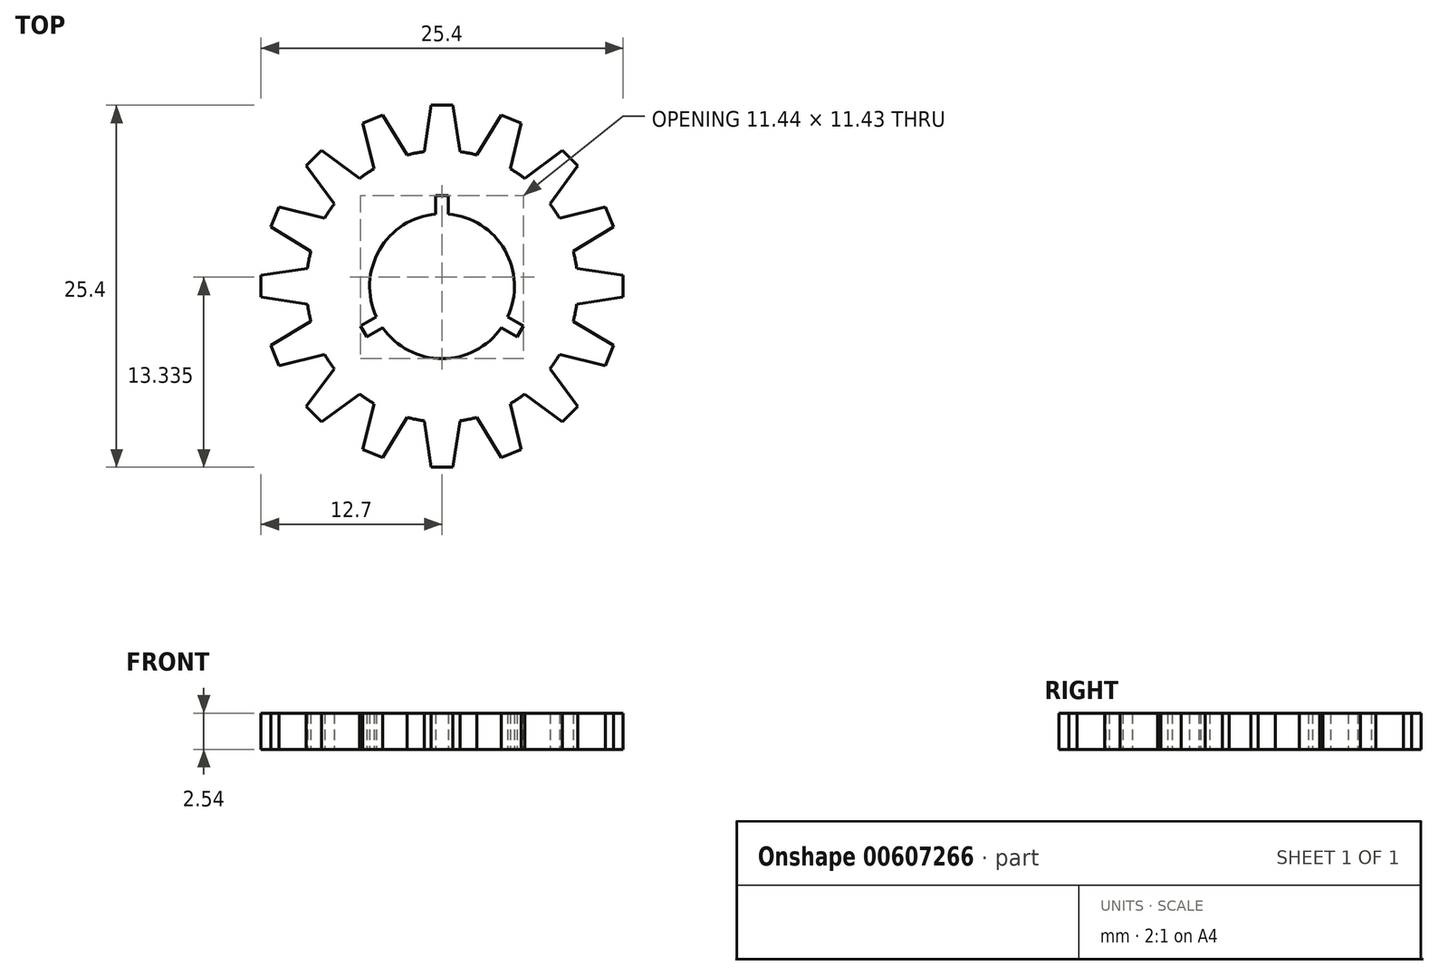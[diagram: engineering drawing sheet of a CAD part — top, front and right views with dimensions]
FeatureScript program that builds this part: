
annotation { "Feature Type Name" : "Feature", "Feature Type Description" : "" }
export const myFeature = defineFeature(function(context is Context, id is Id, definition is map)
    precondition{}
    {
        {
            var Q0;
            Q0=qCreatedBy(makeId("Top.planeOp"),FACE);
            var sketch = newSketch(context, id + "F0", { "sketchPlane" : qUnion([Q0])});
            skArc(sketch, "E0", {"start": v(-7.56, 5.79) * mm, "mid": v(-7.92, 5.3) * mm, "end": v(-8.24, 4.77) * mm});
            skArc(sketch, "E1", {"start": v(-0.44, 5.06) * mm, "mid": v(-4.4, 2.54) * mm, "end": v(-4.6, -2.15) * mm});
            skLineSegment(sketch, "E2", {"start": v(0, 0) * mm, "end": v(0, 6.35) * mm});
            skLineSegment(sketch, "E3", {"start": v(0, 12.7) * mm, "end": v(-0.76, 12.7) * mm});
            skLineSegment(sketch, "E4", {"start": v(-0.76, 12.7) * mm, "end": v(-1.26, 9.44) * mm});
            skLineSegment(sketch, "E5.MirrorCS", {"start": v(0.76, 12.7) * mm, "end": v(1.26, 9.44) * mm});
            skLineSegment(sketch, "E6.MirrorCS", {"start": v(0, 12.7) * mm, "end": v(0.76, 12.7) * mm});
            skLineSegment(sketch, "E7.1.0", {"start": v(-5.56, 11.44) * mm, "end": v(-4.77, 8.24) * mm});
            skLineSegment(sketch, "E7.1.1", {"start": v(-4.16, 12.02) * mm, "end": v(-2.45, 9.2) * mm});
            skLineSegment(sketch, "E7.1.2", {"start": v(-4.86, 11.73) * mm, "end": v(-4.16, 12.02) * mm});
            skLineSegment(sketch, "E7.1.3", {"start": v(-4.86, 11.73) * mm, "end": v(-5.56, 11.44) * mm});
            skLineSegment(sketch, "E7.2.0", {"start": v(-9.52, 8.44) * mm, "end": v(-7.56, 5.79) * mm});
            skLineSegment(sketch, "E7.2.1", {"start": v(-8.44, 9.52) * mm, "end": v(-5.79, 7.56) * mm});
            skLineSegment(sketch, "E7.2.2", {"start": v(-8.98, 8.98) * mm, "end": v(-8.44, 9.52) * mm});
            skLineSegment(sketch, "E7.2.3", {"start": v(-8.98, 8.98) * mm, "end": v(-9.52, 8.44) * mm});
            skLineSegment(sketch, "E7.3.0", {"start": v(-12.02, 4.16) * mm, "end": v(-9.2, 2.45) * mm});
            skLineSegment(sketch, "E7.3.1", {"start": v(-11.44, 5.56) * mm, "end": v(-8.24, 4.77) * mm});
            skLineSegment(sketch, "E7.3.2", {"start": v(-11.73, 4.86) * mm, "end": v(-11.44, 5.56) * mm});
            skLineSegment(sketch, "E7.3.3", {"start": v(-11.73, 4.86) * mm, "end": v(-12.02, 4.16) * mm});
            skLineSegment(sketch, "E7.4.0", {"start": v(-12.7, -0.76) * mm, "end": v(-9.44, -1.26) * mm});
            skLineSegment(sketch, "E7.4.1", {"start": v(-12.7, 0.76) * mm, "end": v(-9.44, 1.26) * mm});
            skLineSegment(sketch, "E7.4.2", {"start": v(-12.7, 0) * mm, "end": v(-12.7, 0.76) * mm});
            skLineSegment(sketch, "E7.4.3", {"start": v(-12.7, 0) * mm, "end": v(-12.7, -0.76) * mm});
            skLineSegment(sketch, "E7.5.0", {"start": v(-11.44, -5.56) * mm, "end": v(-8.24, -4.77) * mm});
            skLineSegment(sketch, "E7.5.1", {"start": v(-12.02, -4.16) * mm, "end": v(-9.2, -2.45) * mm});
            skLineSegment(sketch, "E7.5.2", {"start": v(-11.73, -4.86) * mm, "end": v(-12.02, -4.16) * mm});
            skLineSegment(sketch, "E7.5.3", {"start": v(-11.73, -4.86) * mm, "end": v(-11.44, -5.56) * mm});
            skLineSegment(sketch, "E7.6.0", {"start": v(-8.44, -9.52) * mm, "end": v(-5.79, -7.56) * mm});
            skLineSegment(sketch, "E7.6.1", {"start": v(-9.52, -8.44) * mm, "end": v(-7.56, -5.79) * mm});
            skLineSegment(sketch, "E7.6.2", {"start": v(-8.98, -8.98) * mm, "end": v(-9.52, -8.44) * mm});
            skLineSegment(sketch, "E7.6.3", {"start": v(-8.98, -8.98) * mm, "end": v(-8.44, -9.52) * mm});
            skLineSegment(sketch, "E7.7.0", {"start": v(-4.16, -12.02) * mm, "end": v(-2.45, -9.2) * mm});
            skLineSegment(sketch, "E7.7.1", {"start": v(-5.56, -11.44) * mm, "end": v(-4.77, -8.24) * mm});
            skLineSegment(sketch, "E7.7.2", {"start": v(-4.86, -11.73) * mm, "end": v(-5.56, -11.44) * mm});
            skLineSegment(sketch, "E7.7.3", {"start": v(-4.86, -11.73) * mm, "end": v(-4.16, -12.02) * mm});
            skLineSegment(sketch, "E7.8.0", {"start": v(0.76, -12.7) * mm, "end": v(1.26, -9.44) * mm});
            skLineSegment(sketch, "E7.8.1", {"start": v(-0.76, -12.7) * mm, "end": v(-1.26, -9.44) * mm});
            skLineSegment(sketch, "E7.8.2", {"start": v(0, -12.7) * mm, "end": v(-0.76, -12.7) * mm});
            skLineSegment(sketch, "E7.8.3", {"start": v(0, -12.7) * mm, "end": v(0.76, -12.7) * mm});
            skLineSegment(sketch, "E7.9.0", {"start": v(5.56, -11.44) * mm, "end": v(4.77, -8.24) * mm});
            skLineSegment(sketch, "E7.9.1", {"start": v(4.16, -12.02) * mm, "end": v(2.45, -9.2) * mm});
            skLineSegment(sketch, "E7.9.2", {"start": v(4.86, -11.73) * mm, "end": v(4.16, -12.02) * mm});
            skLineSegment(sketch, "E7.9.3", {"start": v(4.86, -11.73) * mm, "end": v(5.56, -11.44) * mm});
            skLineSegment(sketch, "E7.10.0", {"start": v(9.52, -8.44) * mm, "end": v(7.56, -5.79) * mm});
            skLineSegment(sketch, "E7.10.1", {"start": v(8.44, -9.52) * mm, "end": v(5.79, -7.56) * mm});
            skLineSegment(sketch, "E7.10.2", {"start": v(8.98, -8.98) * mm, "end": v(8.44, -9.52) * mm});
            skLineSegment(sketch, "E7.10.3", {"start": v(8.98, -8.98) * mm, "end": v(9.52, -8.44) * mm});
            skLineSegment(sketch, "E7.11.0", {"start": v(12.02, -4.16) * mm, "end": v(9.2, -2.45) * mm});
            skLineSegment(sketch, "E7.11.1", {"start": v(11.44, -5.56) * mm, "end": v(8.24, -4.77) * mm});
            skLineSegment(sketch, "E7.11.2", {"start": v(11.73, -4.86) * mm, "end": v(11.44, -5.56) * mm});
            skLineSegment(sketch, "E7.11.3", {"start": v(11.73, -4.86) * mm, "end": v(12.02, -4.16) * mm});
            skLineSegment(sketch, "E7.12.0", {"start": v(12.7, 0.76) * mm, "end": v(9.44, 1.26) * mm});
            skLineSegment(sketch, "E7.12.1", {"start": v(12.7, -0.76) * mm, "end": v(9.44, -1.26) * mm});
            skLineSegment(sketch, "E7.12.2", {"start": v(12.7, 0) * mm, "end": v(12.7, -0.76) * mm});
            skLineSegment(sketch, "E7.12.3", {"start": v(12.7, 0) * mm, "end": v(12.7, 0.76) * mm});
            skLineSegment(sketch, "E7.13.0", {"start": v(11.44, 5.56) * mm, "end": v(8.24, 4.77) * mm});
            skLineSegment(sketch, "E7.13.1", {"start": v(12.02, 4.16) * mm, "end": v(9.2, 2.45) * mm});
            skLineSegment(sketch, "E7.13.2", {"start": v(11.73, 4.86) * mm, "end": v(12.02, 4.16) * mm});
            skLineSegment(sketch, "E7.13.3", {"start": v(11.73, 4.86) * mm, "end": v(11.44, 5.56) * mm});
            skLineSegment(sketch, "E7.14.0", {"start": v(8.44, 9.52) * mm, "end": v(5.79, 7.56) * mm});
            skLineSegment(sketch, "E7.14.1", {"start": v(9.52, 8.44) * mm, "end": v(7.56, 5.79) * mm});
            skLineSegment(sketch, "E7.14.2", {"start": v(8.98, 8.98) * mm, "end": v(9.52, 8.44) * mm});
            skLineSegment(sketch, "E7.14.3", {"start": v(8.98, 8.98) * mm, "end": v(8.44, 9.52) * mm});
            skLineSegment(sketch, "E7.15.0", {"start": v(4.16, 12.02) * mm, "end": v(2.45, 9.2) * mm});
            skLineSegment(sketch, "E7.15.1", {"start": v(5.56, 11.44) * mm, "end": v(4.77, 8.24) * mm});
            skLineSegment(sketch, "E7.15.2", {"start": v(4.86, 11.73) * mm, "end": v(5.56, 11.44) * mm});
            skLineSegment(sketch, "E7.15.3", {"start": v(4.86, 11.73) * mm, "end": v(4.16, 12.02) * mm});
            skLineSegment(sketch, "E8.bottom", {"start": v(0.44, 6.35) * mm, "end": v(-0.44, 6.35) * mm});
            skLineSegment(sketch, "E8.left", {"start": v(0.44, 6.35) * mm, "end": v(0.44, 5.06) * mm});
            skLineSegment(sketch, "E8.right", {"start": v(-0.44, 6.35) * mm, "end": v(-0.44, 5.06) * mm});
            skPoint(sketch, "E8.middle", {"position": v(0, 5.08) * mm});
            skPoint(sketch, "E9.orphan", {"position": v(0.44, 3.8) * mm});
            skPoint(sketch, "E10.orphan", {"position": v(-0.44, 3.81) * mm});
            skLineSegment(sketch, "E11.1.0", {"start": v(-5.28, -3.56) * mm, "end": v(-4.16, -2.92) * mm});
            skLineSegment(sketch, "E11.1.1", {"start": v(-5.72, -2.8) * mm, "end": v(-5.28, -3.56) * mm});
            skLineSegment(sketch, "E11.1.2", {"start": v(-5.72, -2.8) * mm, "end": v(-4.6, -2.15) * mm});
            skLineSegment(sketch, "E11.2.0", {"start": v(5.72, -2.8) * mm, "end": v(4.6, -2.15) * mm});
            skLineSegment(sketch, "E11.2.1", {"start": v(5.28, -3.56) * mm, "end": v(5.72, -2.8) * mm});
            skLineSegment(sketch, "E11.2.2", {"start": v(5.28, -3.56) * mm, "end": v(4.16, -2.92) * mm});
            skArc(sketch, "E12.trimOffspring", {"start": v(4.6, -2.15) * mm, "mid": v(4.4, 2.54) * mm, "end": v(0.44, 5.06) * mm});
            skArc(sketch, "E13.trimOffspring", {"start": v(-4.16, -2.92) * mm, "mid": v(0, -5.08) * mm, "end": v(4.16, -2.92) * mm});
            skArc(sketch, "E14.trimOffspring", {"start": v(-4.77, 8.24) * mm, "mid": v(-5.3, 7.92) * mm, "end": v(-5.79, 7.56) * mm});
            skArc(sketch, "E15.trimOffspring", {"start": v(-1.26, 9.44) * mm, "mid": v(-1.86, 9.34) * mm, "end": v(-2.45, 9.2) * mm});
            skArc(sketch, "E16.trimOffspring", {"start": v(2.45, 9.2) * mm, "mid": v(1.86, 9.34) * mm, "end": v(1.26, 9.44) * mm});
            skArc(sketch, "E17.trimOffspring", {"start": v(5.79, 7.56) * mm, "mid": v(5.3, 7.92) * mm, "end": v(4.77, 8.24) * mm});
            skArc(sketch, "E18.trimOffspring", {"start": v(8.24, 4.77) * mm, "mid": v(7.92, 5.3) * mm, "end": v(7.56, 5.79) * mm});
            skArc(sketch, "E19.trimOffspring", {"start": v(9.44, 1.26) * mm, "mid": v(9.34, 1.86) * mm, "end": v(9.2, 2.45) * mm});
            skArc(sketch, "E20.trimOffspring", {"start": v(9.2, -2.45) * mm, "mid": v(9.34, -1.86) * mm, "end": v(9.44, -1.26) * mm});
            skArc(sketch, "E21.trimOffspring", {"start": v(7.56, -5.79) * mm, "mid": v(7.92, -5.3) * mm, "end": v(8.24, -4.77) * mm});
            skArc(sketch, "E22.trimOffspring", {"start": v(4.77, -8.24) * mm, "mid": v(5.3, -7.92) * mm, "end": v(5.79, -7.56) * mm});
            skArc(sketch, "E23.trimOffspring", {"start": v(1.26, -9.44) * mm, "mid": v(1.86, -9.34) * mm, "end": v(2.45, -9.2) * mm});
            skArc(sketch, "E24.trimOffspring", {"start": v(-2.45, -9.2) * mm, "mid": v(-1.86, -9.34) * mm, "end": v(-1.26, -9.44) * mm});
            skArc(sketch, "E25.trimOffspring", {"start": v(-5.79, -7.56) * mm, "mid": v(-5.3, -7.92) * mm, "end": v(-4.77, -8.24) * mm});
            skArc(sketch, "E26.trimOffspring", {"start": v(-8.24, -4.77) * mm, "mid": v(-7.92, -5.3) * mm, "end": v(-7.56, -5.79) * mm});
            skArc(sketch, "E27.trimOffspring", {"start": v(-9.44, -1.26) * mm, "mid": v(-9.34, -1.86) * mm, "end": v(-9.2, -2.45) * mm});
            skArc(sketch, "E28.trimOffspring", {"start": v(-9.2, 2.45) * mm, "mid": v(-9.34, 1.86) * mm, "end": v(-9.44, 1.26) * mm});
            skSolve(sketch);
        }
        {
            var Q0;
            Q0 = qSketchRegion(id + "F0", true);
            extrude(context, id + "F1", {"entities" : qUnion([Q0]), "depth" : 2.54 * mm, "offsetDistance" : 25.4 * mm});
        }
    });
